# Revit family: E-713_RFA
name_source: partatom
category: Aparatos sanitarios
units: mm (PartAtom-declared; Revit-internal decimal feet)

## family parameters
Activar corte en vistas = No
Compartido = Sí
Corte con vacíos al cargar = No
Cota de conector redondo = Usar diámetro
Mantener orientación de anotación = No
Número OmniClass = 23.45.05.14.99
Punto de cálculo de habitación = Sí
Se basa en plano de trabajo = Sí
Siempre vertical = Sí
Tipo de pieza = Normal
Título OmniClass = Other Sanitary Washing Plumbing Fixtures

## types (1)
- E-713
    Altura = 7"
    Ancho = 4"
    Brass Chromed = Brass
    Cartucho = Monomando para regadera o tina sin desviador
con cartucho cerámico de 40mm.
Incluye una caja de instalación rápida con nivel de
profundidad, nivel de burbuja para nivelar en el
plano horizontal y vertical,
conexiones hembra roscadas para eliminar fugas
de conexión.
En caso de fuga el agua se encapsula en el
interior de la caja de instalación y
no se expande al muro, la caja se puede instalar
de dorso contra dorso.
La forma cuadrada de la caja de instalación
permite cortes en ángulo recto.
    Comentarios de tipo = Monomando Máxima
    Descripción = Monomando para Regadera con Desviador.
    Elevación por defecto = 0"
    Fabricante = HELVEX S.A. DE C.V.
    Garantía = El producto HELVEX está garantizado como libre de defectos en materiales y procesos de fabricación. El producto HELVEX está garantizado, en lo que se refiere a los acabados; por un periodo de 10 años en los acabados cromo y duravex, y por 2 años en cabados diferentes al cromo, a partir de la fecha de compra indicada en la factura.
    Imagen de tipo = E-713.jpg
    Instalación = Conxión interna ½" - 14 NPT
    Modelo = E-713
    Operación = Para abrir el flujo de agua levante la palanca maneral y gire para regular la temperatura.
    Presión máxima de trabajo = 85.3 psi
    Presión mínima de trabajo = 14.2 psi
    Profundidad = 5"
    URL = https://helvex.com.mx

## geometry (parser evidence)
native form markers: Sweep x3
no freeform markers — native parametric forms only
